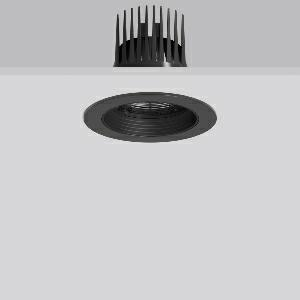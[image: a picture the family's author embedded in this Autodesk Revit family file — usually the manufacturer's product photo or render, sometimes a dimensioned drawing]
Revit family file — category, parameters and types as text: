
# Revit family: heledon_maxi_e_901769_003_3_fede
name_source: partatom
category: Lighting Fixtures
units: mm (PartAtom-declared; Revit-internal decimal feet)

## family parameters
Cut with Voids When Loaded = No
Host = Face
Light Source = No
Part Type = Normal
Room Calculation Point = No
Round Connector Dimension = Use Diameter
Shared = No

## types (1)
- HELEDON maxi E (1 x LED Modul 935, 3650 lm, 3500)
    Apparent Load = 35 VA
    Approval mark = CE
    CIE Flux Codes = 96 100 100 100 100
    Color Rendering = 92
    Color Temperature = 3500
    Default Elevation = 1800 mm
    Description = Series: HELEDON maxi
Round recessed downlight. Housing: die-cast aluminium, powder-coated. Black plastic ring and recessed LED to prevent glare from the side. Optical assembly with lens made of plastic (polycarbonate) for the best homogeneous light distribution - can be changed without tools. Best colour rendering index Ra>90. Suitable for Recessed ceiling mounting. Installation without tools thanks to spring fastening system. Including separate LED converter with connecting cable 600 mm.High quality converter without flickering and stroboscopic effect. Through-wiring box (5 pole) available as accessory. The following accessories can be mounted without use of tools: interchangeable lenses, decorative glasses, honeycomb louvre, clear and frosted diffusers, white interchangeable plastic ring. 
Colour: deep black, matt (RAL 9005)
Diameter: 162 mm
Height: 3 mm
Cut-out diameter: 152 mm
Recess height: 200 mm
Luminaire: recess height: 135 mm
Lamp: LED
Socket: without socket
Colour temperature: 3500K
Colour rendering index (CRI): 92
System power: 35 W
Rated luminous flux: 3650 lm
Luminous efficiency: 104 lm/W
Control gear: Regulated power supply
Protection class: II
Type of protection: IP 20
    Height = 0 mm  [stored 0 ft]
    Lamp = 1 x LED Modul 935
    Lamp Light Flux = 3650 lm
    Lamp count = 1
    Length = 162 mm
    Lifetime = 50000 h
    Luminous efficacy = 104 lm/W
    Manufacturer = RZB
    ModVariant = No
    Model = 901769.003.3
    Mounting Place = Ceiling
    Mounting Type = Recessed
    Number of Poles = 1
    OnlyDefault = Yes
    Power Factor = 1
    Product Name = HELEDON maxi E
    Product group = Recessed downlights
    ProductGroupID = 402
    Protection Class = Protection class II
    Protection Degree = IP 20
    RLX_Detail_Level = 1
    RLX_Emergency_Light_Flux = 0 lm
    RLX_Emergency_Type = 0
    RLX_Emergency_Type_DB = No
    RlxData = <blob elided: 122233 chars, md5=4ec64bb1>
    Socket = socket
    Standby Power = 0 W
    System Light Flux = 3650 lm
    System Power = 35 W
    Type Comments = Product without accessories
    Type Image = 901663.003.jpg
    URL = http://relux.com
    VarID = ---
    Voltage = 230 V
    Voltage Range = 220-240 V
    Weight = 0.00 kg
    Width = 0 mm  [stored 0 ft]

note: [stored X ft] marks values corroborated as IEEE doubles in the binary element streams (Revit-internal decimal feet)

## geometry (parser evidence)
native form markers: Blend x4, Sweep x10
no freeform markers — native parametric forms only
